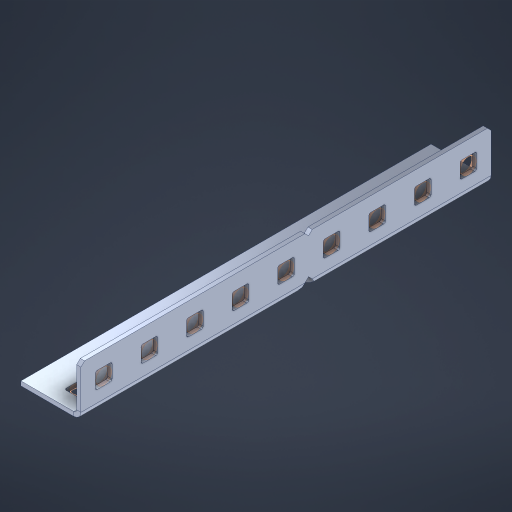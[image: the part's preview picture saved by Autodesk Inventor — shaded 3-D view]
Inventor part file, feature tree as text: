
AUTODESK INVENTOR PART (.ipt)
format: ipt  version: 2023 (Build 270158000, 158)  size: 530,432 bytes
history: native  units: in
note: dims shown in document units (in); Inventor stores cm internally (conversion verified against a paired STEP export)
features: other x23, extrude x17, sheet_metal_op x10, sketch x8, mirror x1, pattern_linear x1, chamfer x1
ambient origin geometry x8: Origin, YZ Plane, XZ Plane, XY Plane, X Axis, Y Axis, Z Axis, Center Point
bodies: Solid1 (feature_tree), Body (feature_tree)
feature tree (61):
  other  "Flange Pattern Plane"
  sheet_metal_op  "Flange Pattern"
  sheet_metal_op  "Body Pattern"
  other  "Arc Length"
  mirror  "Notch Mirror"
  pattern_linear  "Notch Pattern"  Spacing1=0.1875in  [1 undecoded]
  chamfer  "End Chamfer"
  extrude  "Half Cut"  Depth=0.0469in
  sketch  "Sketch1"  dims[d0=2.5in]
  other  "Plate1"
  sketch  "Sketch2"  dims[d1=4.5in]
  other  "Plate2"
  sheet_metal_op  "Bend1"
  sheet_metal_op  "Corner1"
  sketch  "Sketch3"  dims[d2=0.0469in]
  other  "Flange Pattern Sketch"
  sketch  "Sketch7"  dims[d3=0.0469in]
  other  "Srf1"
  other  "Srf2"
  sketch  "Sketch8"  dims[d4=0.0234in]
  sketch  "Sketch9"  dims[d5=0.0938in]
  other  "Srf91"
  sheet_metal_op  "Body Pattern Sketch"
  other  "Srf92"
  sketch  "Sketch13"  dims[d6=0.0469in]
  sketch  "Sketch14"  dims[d7=0.5in d8=90.0deg d9=0.0312in d10=0.1875in d11=0.0469in d12=0.0469in d16=0.182in d17=0.02in d18=0.0469in d19=0.0in d20=0.25in d21=0.25in d46=0.172in d47=1.0in d48=0.0in d49=0.182in d50=0.02in d51=0.25in d52=0.25in d53=0.0469in d54=0.0in d55=0.172in d56=1.0in d57=0.0in d60=3.5433in d62=0.5in d63=0.3937in d65=0.5in d85=0.1227in d86=0.1659in d88=0.04in d89=0.0469in d90=0.0in d91=0.04in d92=0.0491in d95=2.5in d96=0.04in d97=0.25in d98=45.0deg d101=0.0in d102=2.497in d131=0.5in d132=3.5433in d134=0.5in d139=0.5in]
  other  "Srf856"
  other  "Srf1310"
  other  "Srf1311"
  other  "Srf1312"
  other  "Srf1376"
  other  "Srf1377"
  other  "Srf1728"
  other  "Srf1755"
  other  "Srf1878"
  other  "Srf1879"
  other  "Srf1880"
  other  "Srf1942"
  other  "Srf1943"
  other  "Srf1944"
  sheet_metal_op  "Flange Stamp"
  sheet_metal_op  "Flange Circle"
  sheet_metal_op  "Body Stamp"
  sheet_metal_op  "Body Circle"
  sheet_metal_op  "Notch"
  extrude  "ExtrusionSrf2"  Depth=0.0469in
  extrude  "ExtrusionSrf92"  Depth=0.5in
  extrude  "ExtrusionSrf856"  Depth=0.02in
  extrude  "ExtrusionSrf1310"  Depth=0.0469in
  extrude  "ExtrusionSrf1311"  TaperAngle=0.0deg  [1 undecoded]
  extrude  "ExtrusionSrf1312"  Depth=0.5in
  extrude  "ExtrusionSrf1376"  Depth=0.5in
  extrude  "ExtrusionSrf1377"  Depth=0.5in
  extrude  "ExtrusionSrf1728"  Depth=0.5in TaperAngle=0.0deg
  extrude  "ExtrusionSrf1755"  Depth=0.5in
  extrude  "ExtrusionSrf1878"  Depth=0.02in
  extrude  "ExtrusionSrf1879"  Depth=0.5in
  extrude  "ExtrusionSrf1880"  Depth=0.5in
  extrude  "ExtrusionSrf1942"  Depth=0.0469in
  extrude  "ExtrusionSrf1943"  TaperAngle=0.0deg  [1 undecoded]
  extrude  "ExtrusionSrf1944"  Depth=0.5in
note: 3 required parameter values undecoded (feature->parameter linkage not recoverable at this tier; creation-order binding heuristic only, values carry confidence <= 0.55)
